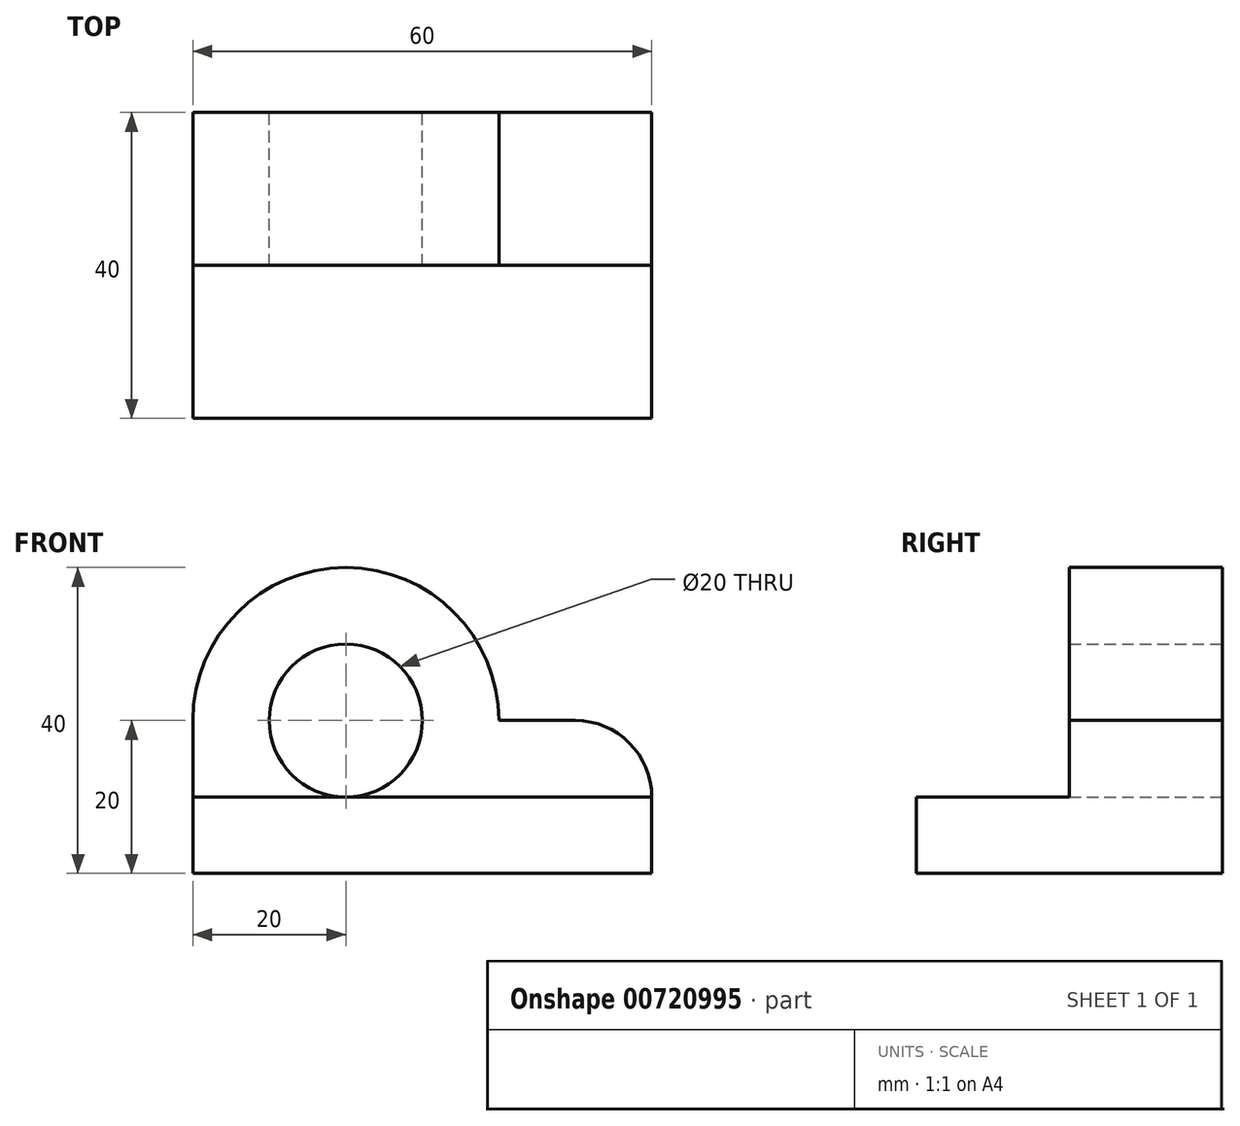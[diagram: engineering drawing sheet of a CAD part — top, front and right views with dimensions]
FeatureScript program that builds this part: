
annotation { "Feature Type Name" : "Feature", "Feature Type Description" : "" }
export const myFeature = defineFeature(function(context is Context, id is Id, definition is map)
    precondition{}
    {
        {
            var Q0;
            Q0=qCreatedBy(makeId("Front.planeOp"),FACE);
            var sketch = newSketch(context, id + "F0", { "sketchPlane" : qUnion([Q0])});
            skLineSegment(sketch, "E0", {"start": v(0, 0) * mm, "end": v(0, 10) * mm});
            skLineSegment(sketch, "E1", {"start": v(0, 0) * mm, "end": v(60, 0) * mm});
            skLineSegment(sketch, "E2", {"start": v(60, 0) * mm, "end": v(60, 10) * mm});
            skLineSegment(sketch, "E3", {"start": v(60, 10) * mm, "end": v(0, 10) * mm});
            skLineSegment(sketch, "E4", {"start": v(0, 10) * mm, "end": v(0, 20) * mm});
            skLineSegment(sketch, "E5", {"start": v(60, 10) * mm, "end": v(60, 10) * mm});
            skLineSegment(sketch, "E6", {"start": v(50, 20) * mm, "end": v(40, 20) * mm});
            skPoint(sketch, "E7.visualSharp", {"position": v(60, 20) * mm});
            skArc(sketch, "E7.filletArc", {"start": v(60, 10) * mm, "mid": v(57.07, 17.07) * mm, "end": v(50, 20) * mm});
            skLineSegment(sketch, "E8", {"start": v(40, 20) * mm, "end": v(0, 20) * mm});
            skLineSegment(sketch, "E9", {"start": v(40, 20) * mm, "end": v(20, 20) * mm});
            skCircle(sketch, "E10", {"center": v(20, 20) * mm, "radius": 20 * mm});
            skCircle(sketch, "E11", {"center": v(20, 20) * mm, "radius": 10 * mm});
            skSolve(sketch);
        }
        {
            var Q0;
            {var subQ0=sQuery(id+"F0.wireOp",EDGE,"E2");Q0=makeQuery(id+"F0.imprint","IMPRINT",FACE,{"disambiguationData":[TD([[makeQuery(id+"F0.imprint","IMPRINT",EDGE,{"derivedFrom":subQ0}),1.0]])]});}
            var Q1;
            {var subQ0=sQuery(id+"F0.wireOp",EDGE,"E0");Q1=makeQuery(id+"F0.imprint","IMPRINT",FACE,{"disambiguationData":[TD([[makeQuery(id+"F0.imprint","IMPRINT",EDGE,{"derivedFrom":subQ0}),-1.0]])]});}
            var Q2;
            {var subQ0=sQuery(id+"F0.wireOp",EDGE,"E10");var subQ1=sQuery(id+"F0.wireOp",EDGE,"E3");var subQ2=makeQuery(id+"F0.imprint","INTERSECT",VERTEX,{"disambiguationData":[OD(0.0)],"derivedFrom":[subQ1,subQ0]});Q2=makeQuery(id+"F0.imprint","IMPRINT",FACE,{"disambiguationData":[TD([[makeQuery(id+"F0.imprint","IMPRINT",EDGE,{"disambiguationData":[TD([[subQ2,-1.0]])],"derivedFrom":subQ1}),1.0]])]});}
            extrude(context, id + "F1", {"entities" : qUnion([Q0, Q1, Q2]), "depth" : 40 * mm, "offsetDistance" : 25 * mm});
        }
        {
            var Q0;
            Q0=qSketchRegion(id+"F0",true);
            extrude(context, id + "F2", {"entities" : qUnion([Q0]), "operationType" : NewBodyOperationType.ADD, "depth" : 20 * mm, "offsetDistance" : 25 * mm});
        }
    });
